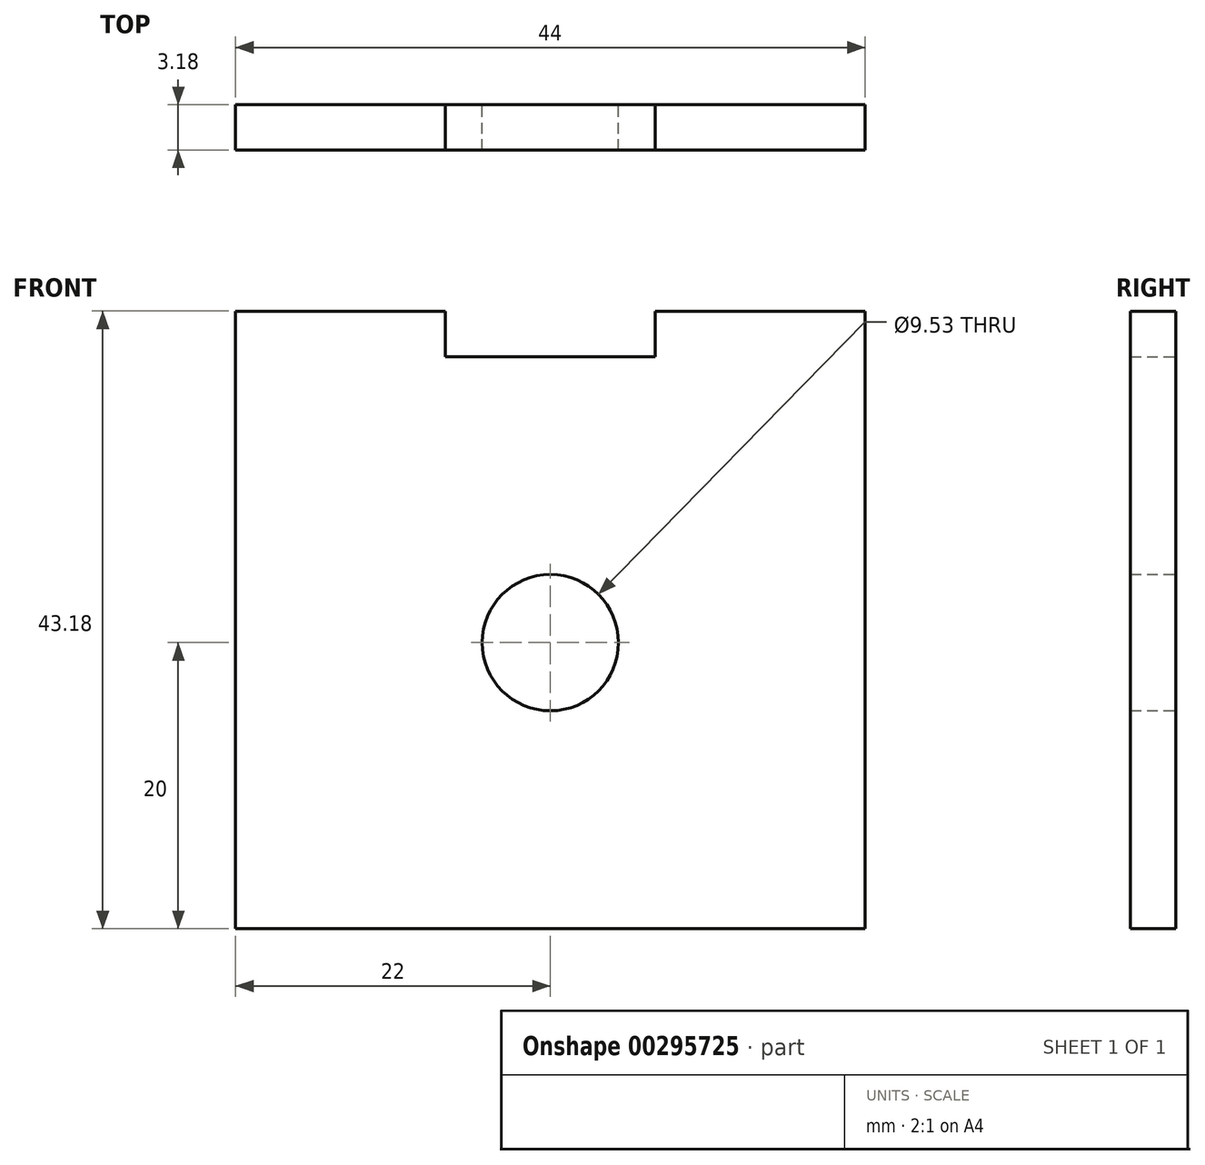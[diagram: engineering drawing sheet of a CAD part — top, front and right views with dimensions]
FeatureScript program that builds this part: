
annotation { "Feature Type Name" : "Feature", "Feature Type Description" : "" }
export const myFeature = defineFeature(function(context is Context, id is Id, definition is map)
    precondition{}
    {
        {
            var Q0;
            Q0=qCreatedBy(makeId("Front.planeOp"),FACE);
            var sketch = newSketch(context, id + "F0", { "sketchPlane" : qUnion([Q0])});
            skCircle(sketch, "E0", {"center": v(0, 0) * mm, "radius": 4.76 * mm});
            skLineSegment(sketch, "E1.bottom", {"start": v(22, -20) * mm, "end": v(-22, -20) * mm});
            skLineSegment(sketch, "E1.top", {"start": v(22, 20) * mm, "end": v(-22, 20) * mm});
            skLineSegment(sketch, "E1.left", {"start": v(22, -20) * mm, "end": v(22, 20) * mm});
            skLineSegment(sketch, "E1.right", {"start": v(-22, -20) * mm, "end": v(-22, 20) * mm});
            skSolve(sketch);
        }
        {
            var Q0;
            Q0=qSketchRegion(id+"F0",true);
            extrude(context, id + "F1", {"entities" : qUnion([Q0]), "depth" : 3.17 * mm});
        }
        {
            var Q0;
            Q0=makeQuery(id+"F1.opExtrude","SWEPT_FACE",FACE,{"disambiguationData":[OSD([sQuery(id+"F0.wireOp",EDGE,"E1.top")])]});
            var sketch = newSketch(context, id + "F2", { "sketchPlane" : qUnion([Q0])});
            skLineSegment(sketch, "E2.bottom", {"start": v(-22, 0) * mm, "end": v(-7.33, 0) * mm});
            skLineSegment(sketch, "E2.top", {"start": v(-22, -3.18) * mm, "end": v(-7.33, -3.18) * mm});
            skLineSegment(sketch, "E2.left", {"start": v(-22, 0) * mm, "end": v(-22, -3.18) * mm});
            skLineSegment(sketch, "E2.right", {"start": v(-7.33, 0) * mm, "end": v(-7.33, -3.18) * mm});
            skLineSegment(sketch, "E3.bottom", {"start": v(-7.33, -3.18) * mm, "end": v(7.33, -3.18) * mm});
            skLineSegment(sketch, "E3.top", {"start": v(-7.33, 0) * mm, "end": v(7.33, 0) * mm});
            skLineSegment(sketch, "E3.left", {"start": v(-7.33, -3.18) * mm, "end": v(-7.33, 0) * mm});
            skLineSegment(sketch, "E3.right", {"start": v(7.33, -3.18) * mm, "end": v(7.33, 0) * mm});
            skLineSegment(sketch, "E4.bottom", {"start": v(7.33, 0) * mm, "end": v(22, 0) * mm});
            skLineSegment(sketch, "E4.top", {"start": v(7.33, -3.18) * mm, "end": v(22, -3.18) * mm});
            skLineSegment(sketch, "E4.left", {"start": v(7.33, 0) * mm, "end": v(7.33, -3.18) * mm});
            skLineSegment(sketch, "E4.right", {"start": v(22, 0) * mm, "end": v(22, -3.18) * mm});
            skSolve(sketch);
        }
        {
            var Q0;
            Q0=makeQuery(id+"F2.imprint","IMPRINT",FACE,{"disambiguationData":[TD([[makeQuery(id+"F2.imprint","IMPRINT",EDGE,{"derivedFrom":sQuery(id+"F2.wireOp",EDGE,"E2.bottom")}),1.0]])]});
            var Q1;
            Q1=makeQuery(id+"F2.imprint","IMPRINT",FACE,{"disambiguationData":[TD([[makeQuery(id+"F2.imprint","IMPRINT",EDGE,{"derivedFrom":sQuery(id+"F2.wireOp",EDGE,"E4.bottom")}),1.0]])]});
            extrude(context, id + "F3", {"entities" : qUnion([Q0, Q1]), "operationType" : NewBodyOperationType.ADD, "depth" : 3.17 * mm});
        }
    });
